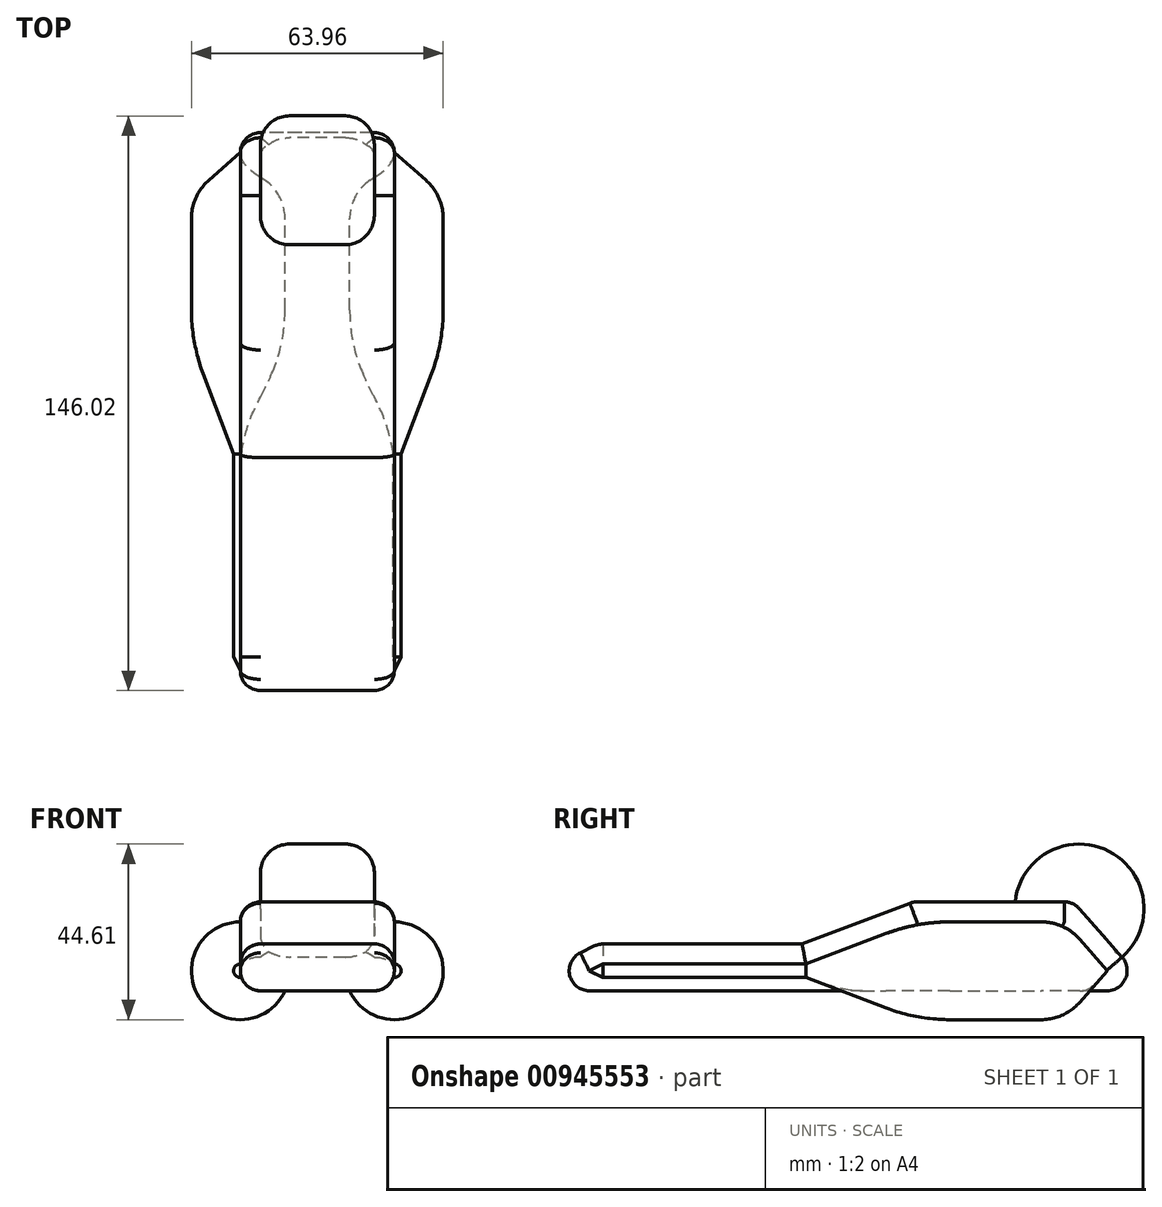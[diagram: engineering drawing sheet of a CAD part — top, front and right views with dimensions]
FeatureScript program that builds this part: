
annotation { "Feature Type Name" : "Feature", "Feature Type Description" : "" }
export const myFeature = defineFeature(function(context is Context, id is Id, definition is map)
    precondition{}
    {
        {
            var Q0;
            Q0=qCreatedBy(makeId("Right.planeOp"),FACE);
            var sketch = newSketch(context, id + "F0", { "sketchPlane" : qUnion([Q0])});
            skLineSegment(sketch, "E0", {"start": v(-69.01, 0) * mm, "end": v(-59.28, 4.77) * mm});
            skLineSegment(sketch, "E1", {"start": v(-59.28, 4.77) * mm, "end": v(-7.5, 4.77) * mm});
            skLineSegment(sketch, "E2", {"start": v(-7.5, 4.77) * mm, "end": v(20.73, 15.48) * mm});
            skLineSegment(sketch, "E3", {"start": v(20.73, 15.48) * mm, "end": v(61.42, 15.48) * mm});
            skLineSegment(sketch, "E4", {"start": v(61.42, 15.48) * mm, "end": v(75.05, 0) * mm});
            skLineSegment(sketch, "E5", {"start": v(75.05, 0) * mm, "end": v(75.05, -7.1) * mm});
            skLineSegment(sketch, "E6", {"start": v(75.05, -7.1) * mm, "end": v(-74.66, -7.1) * mm});
            skLineSegment(sketch, "E7", {"start": v(-74.66, -7.1) * mm, "end": v(-69.01, 0) * mm});
            skSolve(sketch);
        }
        {
            var Q0;
            Q0=makeQuery(id+"F0.imprint","IMPRINT",FACE,{"disambiguationData":[TD([[makeQuery(id+"F0.imprint","IMPRINT",EDGE,{"derivedFrom":sQuery(id+"F0.wireOp",EDGE,"E0")}),-1.0]])]});
            extrude(context, id + "F1", {"entities" : qUnion([Q0]), "depth" : 39.12 * mm, "offsetDistance" : 25.4 * mm});
        }
        {
            var Q0;
            Q0=makeQuery(id+"F1.opExtrude","CAP_EDGE",EDGE,{"disambiguationData":[OSD([sQuery(id+"F0.wireOp",EDGE,"E2")])],"isStart":false});
            fillet(context, id + "F2", {"entities" : qUnion([Q0]), "radius" : 5.08 * mm, "tangentPropagation" : true, "allowEdgeOverflow" : false});
        }
        {
            var Q0;
            Q0=makeQuery(id+"F1.opExtrude","CAP_EDGE",EDGE,{"disambiguationData":[OSD([sQuery(id+"F0.wireOp",EDGE,"E2")])],"isStart":true});
            fillet(context, id + "F3", {"entities" : qUnion([Q0]), "radius" : 5.08 * mm, "tangentPropagation" : true, "allowEdgeOverflow" : false});
        }
        {
            var Q0;
            Q0=makeQuery(id+"F1.opExtrude","SWEPT_EDGE",EDGE,{"disambiguationData":[OSD([sQuery(id+"F0.wireOp",EDGE,"E2"),sQuery(id+"F0.wireOp",EDGE,"E3")])]});
            fillet(context, id + "F4", {"entities" : qUnion([Q0]), "radius" : 5.08 * mm, "tangentPropagation" : true, "allowEdgeOverflow" : false});
        }
        {
            var Q0;
            Q0=makeQuery(id+"F1.opExtrude","CAP_EDGE",EDGE,{"disambiguationData":[OSD([sQuery(id+"F0.wireOp",EDGE,"E1")])],"isStart":true});
            fillet(context, id + "F5", {"entities" : qUnion([Q0]), "radius" : 5.08 * mm, "tangentPropagation" : true, "allowEdgeOverflow" : false});
        }
        {
            var Q0;
            Q0=makeQuery(id+"F5.opFillet","BLEND_EDGE",EDGE,{"blendedFrom":[makeQuery(id+"F1.opExtrude","CAP_EDGE",EDGE,{"disambiguationData":[OSD([sQuery(id+"F0.wireOp",EDGE,"E1")])],"isStart":true}),makeQuery(id+"F1.opExtrude","SWEPT_FACE",FACE,{"disambiguationData":[OSD([sQuery(id+"F0.wireOp",EDGE,"E0")])]})],"blendedInto":[makeQuery(id+"F1.opExtrude","SWEPT_FACE",FACE,{"disambiguationData":[OSD([sQuery(id+"F0.wireOp",EDGE,"E0")])]})]});
            fillet(context, id + "F6", {"entities" : qUnion([Q0]), "radius" : 5.08 * mm, "tangentPropagation" : true, "allowEdgeOverflow" : false});
        }
        {
            var Q0;
            Q0=makeQuery(id+"F6.opFillet","BLEND_EDGE",EDGE,{"blendedFrom":[makeQuery(id+"F5.opFillet","BLEND_EDGE",EDGE,{"blendedFrom":[makeQuery(id+"F1.opExtrude","CAP_EDGE",EDGE,{"disambiguationData":[OSD([sQuery(id+"F0.wireOp",EDGE,"E1")])],"isStart":true}),makeQuery(id+"F1.opExtrude","SWEPT_FACE",FACE,{"disambiguationData":[OSD([sQuery(id+"F0.wireOp",EDGE,"E0")])]})],"blendedInto":[makeQuery(id+"F1.opExtrude","SWEPT_FACE",FACE,{"disambiguationData":[OSD([sQuery(id+"F0.wireOp",EDGE,"E0")])]})]}),makeQuery(id+"F1.opExtrude","SWEPT_FACE",FACE,{"disambiguationData":[OSD([sQuery(id+"F0.wireOp",EDGE,"E7")])]})],"blendedInto":[makeQuery(id+"F1.opExtrude","SWEPT_FACE",FACE,{"disambiguationData":[OSD([sQuery(id+"F0.wireOp",EDGE,"E7")])]})]});
            fillet(context, id + "F7", {"entities" : qUnion([Q0]), "radius" : 5.08 * mm, "tangentPropagation" : true, "allowEdgeOverflow" : false});
        }
        {
            var Q0;
            Q0=makeQuery(id+"F1.opExtrude","CAP_EDGE",EDGE,{"disambiguationData":[OSD([sQuery(id+"F0.wireOp",EDGE,"E1")])],"isStart":false});
            fillet(context, id + "F8", {"entities" : qUnion([Q0]), "radius" : 5.08 * mm, "tangentPropagation" : true, "allowEdgeOverflow" : false});
        }
        {
            var Q0;
            Q0=makeQuery(id+"F1.opExtrude","SWEPT_EDGE",EDGE,{"disambiguationData":[OSD([sQuery(id+"F0.wireOp",EDGE,"E3"),sQuery(id+"F0.wireOp",EDGE,"E4")])]});
            fillet(context, id + "F9", {"entities" : qUnion([Q0]), "radius" : 5.08 * mm, "tangentPropagation" : true, "allowEdgeOverflow" : false});
        }
        {
            var Q0;
            Q0=makeQuery(id+"F1.opExtrude","SWEPT_EDGE",EDGE,{"disambiguationData":[OSD([sQuery(id+"F0.wireOp",EDGE,"E5"),sQuery(id+"F0.wireOp",EDGE,"E6")])]});
            fillet(context, id + "F10", {"entities" : qUnion([Q0]), "radius" : 5.08 * mm, "tangentPropagation" : true, "allowEdgeOverflow" : false});
        }
        {
            var Q0;
            Q0=makeQuery(id+"F1.opExtrude","CAP_EDGE",EDGE,{"disambiguationData":[OSD([sQuery(id+"F0.wireOp",EDGE,"E6")])],"isStart":false});
            fillet(context, id + "F11", {"entities" : qUnion([Q0]), "radius" : 5.08 * mm, "tangentPropagation" : true, "allowEdgeOverflow" : false});
        }
        {
            var Q0;
            Q0=makeQuery(id+"F1.opExtrude","CAP_FACE",FACE,{"disambiguationData":[OSD([sQuery(id+"F0.wireOp",EDGE,"E0"),sQuery(id+"F0.wireOp",EDGE,"E1"),sQuery(id+"F0.wireOp",EDGE,"E2"),sQuery(id+"F0.wireOp",EDGE,"E3"),sQuery(id+"F0.wireOp",EDGE,"E4"),sQuery(id+"F0.wireOp",EDGE,"E5"),sQuery(id+"F0.wireOp",EDGE,"E6"),sQuery(id+"F0.wireOp",EDGE,"E7")])],"isStart":true});
            var Q1;
            {var subQ0=sQuery(id+"F0.wireOp",EDGE,"E6");Q1=makeQuery(id+"F11.opFillet","BLEND_EDGE",EDGE,{"blendedFrom":[makeQuery(id+"F1.opExtrude","CAP_EDGE",EDGE,{"disambiguationData":[OSD([subQ0])],"isStart":true}),makeQuery(id+"F1.opExtrude","CAP_FACE",FACE,{"disambiguationData":[OSD([sQuery(id+"F0.wireOp",EDGE,"E0"),sQuery(id+"F0.wireOp",EDGE,"E1"),sQuery(id+"F0.wireOp",EDGE,"E2"),sQuery(id+"F0.wireOp",EDGE,"E3"),sQuery(id+"F0.wireOp",EDGE,"E4"),sQuery(id+"F0.wireOp",EDGE,"E5"),subQ0,sQuery(id+"F0.wireOp",EDGE,"E7")])],"isStart":true})],"blendedInto":[makeQuery(id+"F1.opExtrude","CAP_FACE",FACE,{"disambiguationData":[OSD([sQuery(id+"F0.wireOp",EDGE,"E0"),sQuery(id+"F0.wireOp",EDGE,"E1"),sQuery(id+"F0.wireOp",EDGE,"E2"),sQuery(id+"F0.wireOp",EDGE,"E3"),sQuery(id+"F0.wireOp",EDGE,"E4"),sQuery(id+"F0.wireOp",EDGE,"E5"),subQ0,sQuery(id+"F0.wireOp",EDGE,"E7")])],"isStart":true})]});}
            revolve(context, id + "F12", {"operationType" : NewBodyOperationType.ADD, "surfaceOperationType" : NewSurfaceOperationType.NEW, "entities" : qUnion([Q0]), "axis" : qUnion([Q1]), "revolveType" : RevolveType.FULL});
        }
        {
            var Q0;
            Q0=makeQuery(id+"F1.opExtrude","CAP_FACE",FACE,{"disambiguationData":[OSD([sQuery(id+"F0.wireOp",EDGE,"E0"),sQuery(id+"F0.wireOp",EDGE,"E1"),sQuery(id+"F0.wireOp",EDGE,"E2"),sQuery(id+"F0.wireOp",EDGE,"E3"),sQuery(id+"F0.wireOp",EDGE,"E4"),sQuery(id+"F0.wireOp",EDGE,"E5"),sQuery(id+"F0.wireOp",EDGE,"E6"),sQuery(id+"F0.wireOp",EDGE,"E7")])],"isStart":false});
            var Q1;
            {var subQ0=sQuery(id+"F0.wireOp",EDGE,"E6");Q1=makeQuery(id+"F11.opFillet","BLEND_EDGE",EDGE,{"blendedFrom":[makeQuery(id+"F1.opExtrude","CAP_EDGE",EDGE,{"disambiguationData":[OSD([subQ0])],"isStart":false}),makeQuery(id+"F1.opExtrude","CAP_FACE",FACE,{"disambiguationData":[OSD([sQuery(id+"F0.wireOp",EDGE,"E0"),sQuery(id+"F0.wireOp",EDGE,"E1"),sQuery(id+"F0.wireOp",EDGE,"E2"),sQuery(id+"F0.wireOp",EDGE,"E3"),sQuery(id+"F0.wireOp",EDGE,"E4"),sQuery(id+"F0.wireOp",EDGE,"E5"),subQ0,sQuery(id+"F0.wireOp",EDGE,"E7")])],"isStart":false})],"blendedInto":[makeQuery(id+"F1.opExtrude","CAP_FACE",FACE,{"disambiguationData":[OSD([sQuery(id+"F0.wireOp",EDGE,"E0"),sQuery(id+"F0.wireOp",EDGE,"E1"),sQuery(id+"F0.wireOp",EDGE,"E2"),sQuery(id+"F0.wireOp",EDGE,"E3"),sQuery(id+"F0.wireOp",EDGE,"E4"),sQuery(id+"F0.wireOp",EDGE,"E5"),subQ0,sQuery(id+"F0.wireOp",EDGE,"E7")])],"isStart":false})]});}
            revolve(context, id + "F13", {"operationType" : NewBodyOperationType.ADD, "surfaceOperationType" : NewSurfaceOperationType.NEW, "entities" : qUnion([Q0]), "axis" : qUnion([Q1]), "revolveType" : RevolveType.FULL});
        }
        {
            var Q0;
            {var subQ0=sQuery(id+"F0.wireOp",EDGE,"E7");var subQ1=sQuery(id+"F0.wireOp",EDGE,"E6");var subQ2=sQuery(id+"F0.wireOp",EDGE,"E5");var subQ3=sQuery(id+"F0.wireOp",EDGE,"E4");var subQ4=sQuery(id+"F0.wireOp",EDGE,"E3");var subQ5=sQuery(id+"F0.wireOp",EDGE,"E2");var subQ6=sQuery(id+"F0.wireOp",EDGE,"E1");var subQ7=sQuery(id+"F0.wireOp",EDGE,"E0");Q0=makeQuery(id+"F12.opRevolve","SWEPT_EDGE",EDGE,{"disambiguationData":[OSD([subQ7,subQ6,subQ5,subQ4,subQ3,subQ2,subQ1,subQ0]),TDD([makeQuery(id+"F4.opFillet","BLEND_VERTEX",VERTEX,{"blendedFrom":[makeQuery(id+"F3.opFillet","BLEND_EDGE",EDGE,{"blendedFrom":[makeQuery(id+"F1.opExtrude","CAP_EDGE",EDGE,{"disambiguationData":[OSD([subQ5])],"isStart":true}),makeQuery(id+"F1.opExtrude","SWEPT_FACE",FACE,{"disambiguationData":[OSD([subQ4])]})],"blendedInto":[makeQuery(id+"F1.opExtrude","SWEPT_FACE",FACE,{"disambiguationData":[OSD([subQ4])]})]}),makeQuery(id+"F1.opExtrude","CAP_EDGE",EDGE,{"disambiguationData":[OSD([subQ4])],"isStart":true}),makeQuery(id+"F3.opFillet","BLEND_FACE",FACE,{"disambiguationData":[OSD([subQ5])]}),makeQuery(id+"F1.opExtrude","CAP_FACE",FACE,{"disambiguationData":[OSD([subQ7,subQ6,subQ5,subQ4,subQ3,subQ2,subQ1,subQ0])],"isStart":true})],"blendedInto":[makeQuery(id+"F3.opFillet","BLEND_FACE",FACE,{"disambiguationData":[OSD([subQ5])]}),makeQuery(id+"F1.opExtrude","CAP_FACE",FACE,{"disambiguationData":[OSD([subQ7,subQ6,subQ5,subQ4,subQ3,subQ2,subQ1,subQ0])],"isStart":true})]})])]});}
            fillet(context, id + "F14", {"entities" : qUnion([Q0]), "radius" : 45.74 * mm, "tangentPropagation" : true, "allowEdgeOverflow" : false});
        }
        {
            var Q0;
            {var subQ0=sQuery(id+"F0.wireOp",EDGE,"E7");var subQ1=sQuery(id+"F0.wireOp",EDGE,"E6");var subQ2=sQuery(id+"F0.wireOp",EDGE,"E5");var subQ3=sQuery(id+"F0.wireOp",EDGE,"E4");var subQ4=sQuery(id+"F0.wireOp",EDGE,"E3");var subQ5=sQuery(id+"F0.wireOp",EDGE,"E2");var subQ6=sQuery(id+"F0.wireOp",EDGE,"E1");var subQ7=sQuery(id+"F0.wireOp",EDGE,"E0");var subQ8=makeQuery(id+"F1.opExtrude","CAP_EDGE",EDGE,{"disambiguationData":[OSD([subQ4])],"isStart":true});Q0=makeQuery(id+"F12.opRevolve","SWEPT_EDGE",EDGE,{"disambiguationData":[OSD([subQ7,subQ6,subQ5,subQ4,subQ3,subQ2,subQ1,subQ0]),TDD([makeQuery(id+"F9.opFillet","BLEND_VERTEX",VERTEX,{"blendedFrom":[makeQuery(id+"F1.opExtrude","CAP_EDGE",EDGE,{"disambiguationData":[OSD([subQ3])],"isStart":true}),makeQuery(id+"F4.opFillet","BLEND_EDGE",EDGE,{"blendedFrom":[subQ8,makeQuery(id+"F1.opExtrude","SWEPT_FACE",FACE,{"disambiguationData":[OSD([subQ3])]})],"blendedInto":[makeQuery(id+"F1.opExtrude","SWEPT_FACE",FACE,{"disambiguationData":[OSD([subQ3])]})]}),makeQuery(id+"F4.opFillet","BLEND_FACE",FACE,{"disambiguationData":[OSD([subQ4]),TDD([subQ8])]}),makeQuery(id+"F1.opExtrude","CAP_FACE",FACE,{"disambiguationData":[OSD([subQ7,subQ6,subQ5,subQ4,subQ3,subQ2,subQ1,subQ0])],"isStart":true})],"blendedInto":[makeQuery(id+"F4.opFillet","BLEND_FACE",FACE,{"disambiguationData":[OSD([subQ4]),TDD([subQ8])]}),makeQuery(id+"F1.opExtrude","CAP_FACE",FACE,{"disambiguationData":[OSD([subQ7,subQ6,subQ5,subQ4,subQ3,subQ2,subQ1,subQ0])],"isStart":true})]})])]});}
            fillet(context, id + "F15", {"entities" : qUnion([Q0]), "radius" : 13.04 * mm, "tangentPropagation" : true, "allowEdgeOverflow" : false});
        }
        {
            var Q0;
            {var subQ0=sQuery(id+"F0.wireOp",EDGE,"E7");var subQ1=sQuery(id+"F0.wireOp",EDGE,"E6");var subQ2=sQuery(id+"F0.wireOp",EDGE,"E5");var subQ3=sQuery(id+"F0.wireOp",EDGE,"E4");var subQ4=sQuery(id+"F0.wireOp",EDGE,"E3");var subQ5=sQuery(id+"F0.wireOp",EDGE,"E2");var subQ6=sQuery(id+"F0.wireOp",EDGE,"E1");var subQ7=sQuery(id+"F0.wireOp",EDGE,"E0");Q0=makeQuery(id+"F12.opRevolve","SWEPT_EDGE",EDGE,{"disambiguationData":[OSD([subQ7,subQ6,subQ5,subQ4,subQ3,subQ2,subQ1,subQ0]),TDD([makeQuery(id+"F6.opFillet","BLEND_VERTEX",VERTEX,{"blendedFrom":[makeQuery(id+"F5.opFillet","BLEND_EDGE",EDGE,{"blendedFrom":[makeQuery(id+"F1.opExtrude","CAP_EDGE",EDGE,{"disambiguationData":[OSD([subQ6])],"isStart":true}),makeQuery(id+"F1.opExtrude","SWEPT_FACE",FACE,{"disambiguationData":[OSD([subQ7])]})],"blendedInto":[makeQuery(id+"F1.opExtrude","SWEPT_FACE",FACE,{"disambiguationData":[OSD([subQ7])]})]}),makeQuery(id+"F5.opFillet","BLEND_FACE",FACE,{"disambiguationData":[OSD([subQ6])]}),makeQuery(id+"F1.opExtrude","CAP_FACE",FACE,{"disambiguationData":[OSD([subQ7,subQ6,subQ5,subQ4,subQ3,subQ2,subQ1,subQ0])],"isStart":true})],"blendedInto":[makeQuery(id+"F5.opFillet","BLEND_FACE",FACE,{"disambiguationData":[OSD([subQ6])]}),makeQuery(id+"F1.opExtrude","CAP_FACE",FACE,{"disambiguationData":[OSD([subQ7,subQ6,subQ5,subQ4,subQ3,subQ2,subQ1,subQ0])],"isStart":true})]})])]});}
            fillet(context, id + "F16", {"entities" : qUnion([Q0]), "radius" : 0.38 * mm, "tangentPropagation" : true, "allowEdgeOverflow" : false});
        }
        {
            var Q0;
            {var subQ0=sQuery(id+"F0.wireOp",EDGE,"E7");var subQ1=sQuery(id+"F0.wireOp",EDGE,"E6");var subQ2=sQuery(id+"F0.wireOp",EDGE,"E5");var subQ3=sQuery(id+"F0.wireOp",EDGE,"E4");var subQ4=sQuery(id+"F0.wireOp",EDGE,"E3");var subQ5=sQuery(id+"F0.wireOp",EDGE,"E2");var subQ6=sQuery(id+"F0.wireOp",EDGE,"E1");var subQ7=sQuery(id+"F0.wireOp",EDGE,"E0");Q0=makeQuery(id+"F13.opRevolve","SWEPT_EDGE",EDGE,{"disambiguationData":[OSD([subQ7,subQ6,subQ5,subQ4,subQ3,subQ2,subQ1,subQ0]),TDD([makeQuery(id+"F4.opFillet","BLEND_VERTEX",VERTEX,{"blendedFrom":[makeQuery(id+"F2.opFillet","BLEND_EDGE",EDGE,{"blendedFrom":[makeQuery(id+"F1.opExtrude","CAP_EDGE",EDGE,{"disambiguationData":[OSD([subQ5])],"isStart":false}),makeQuery(id+"F1.opExtrude","SWEPT_FACE",FACE,{"disambiguationData":[OSD([subQ4])]})],"blendedInto":[makeQuery(id+"F1.opExtrude","SWEPT_FACE",FACE,{"disambiguationData":[OSD([subQ4])]})]}),makeQuery(id+"F1.opExtrude","CAP_EDGE",EDGE,{"disambiguationData":[OSD([subQ4])],"isStart":false}),makeQuery(id+"F2.opFillet","BLEND_FACE",FACE,{"disambiguationData":[OSD([subQ5])]}),makeQuery(id+"F1.opExtrude","CAP_FACE",FACE,{"disambiguationData":[OSD([subQ7,subQ6,subQ5,subQ4,subQ3,subQ2,subQ1,subQ0])],"isStart":false})],"blendedInto":[makeQuery(id+"F2.opFillet","BLEND_FACE",FACE,{"disambiguationData":[OSD([subQ5])]}),makeQuery(id+"F1.opExtrude","CAP_FACE",FACE,{"disambiguationData":[OSD([subQ7,subQ6,subQ5,subQ4,subQ3,subQ2,subQ1,subQ0])],"isStart":false})]})])]});}
            fillet(context, id + "F17", {"entities" : qUnion([Q0]), "radius" : 45.74 * mm, "tangentPropagation" : true, "allowEdgeOverflow" : false});
        }
        {
            var Q0;
            {var subQ0=sQuery(id+"F0.wireOp",EDGE,"E7");var subQ1=sQuery(id+"F0.wireOp",EDGE,"E6");var subQ2=sQuery(id+"F0.wireOp",EDGE,"E5");var subQ3=sQuery(id+"F0.wireOp",EDGE,"E4");var subQ4=sQuery(id+"F0.wireOp",EDGE,"E3");var subQ5=sQuery(id+"F0.wireOp",EDGE,"E2");var subQ6=sQuery(id+"F0.wireOp",EDGE,"E1");var subQ7=sQuery(id+"F0.wireOp",EDGE,"E0");var subQ8=makeQuery(id+"F1.opExtrude","CAP_EDGE",EDGE,{"disambiguationData":[OSD([subQ4])],"isStart":false});Q0=makeQuery(id+"F13.opRevolve","SWEPT_EDGE",EDGE,{"disambiguationData":[OSD([subQ7,subQ6,subQ5,subQ4,subQ3,subQ2,subQ1,subQ0]),TDD([makeQuery(id+"F9.opFillet","BLEND_VERTEX",VERTEX,{"blendedFrom":[makeQuery(id+"F1.opExtrude","CAP_EDGE",EDGE,{"disambiguationData":[OSD([subQ3])],"isStart":false}),makeQuery(id+"F4.opFillet","BLEND_EDGE",EDGE,{"blendedFrom":[subQ8,makeQuery(id+"F1.opExtrude","SWEPT_FACE",FACE,{"disambiguationData":[OSD([subQ3])]})],"blendedInto":[makeQuery(id+"F1.opExtrude","SWEPT_FACE",FACE,{"disambiguationData":[OSD([subQ3])]})]}),makeQuery(id+"F4.opFillet","BLEND_FACE",FACE,{"disambiguationData":[OSD([subQ4]),TDD([subQ8])]}),makeQuery(id+"F1.opExtrude","CAP_FACE",FACE,{"disambiguationData":[OSD([subQ7,subQ6,subQ5,subQ4,subQ3,subQ2,subQ1,subQ0])],"isStart":false})],"blendedInto":[makeQuery(id+"F4.opFillet","BLEND_FACE",FACE,{"disambiguationData":[OSD([subQ4]),TDD([subQ8])]}),makeQuery(id+"F1.opExtrude","CAP_FACE",FACE,{"disambiguationData":[OSD([subQ7,subQ6,subQ5,subQ4,subQ3,subQ2,subQ1,subQ0])],"isStart":false})]})])]});}
            fillet(context, id + "F18", {"entities" : qUnion([Q0]), "radius" : 13.04 * mm, "tangentPropagation" : true, "allowEdgeOverflow" : false});
        }
        {
            var Q0;
            Q0=makeQuery(id+"F1.opExtrude","SWEPT_FACE",FACE,{"disambiguationData":[OSD([sQuery(id+"F0.wireOp",EDGE,"E4")])]});
            var Q1;
            {var subQ0=sQuery(id+"F0.wireOp",EDGE,"E4");Q1=makeQuery(id+"F9.opFillet","BLEND_EDGE",EDGE,{"blendedFrom":[makeQuery(id+"F1.opExtrude","SWEPT_EDGE",EDGE,{"disambiguationData":[OSD([sQuery(id+"F0.wireOp",EDGE,"E3"),subQ0])]}),makeQuery(id+"F1.opExtrude","SWEPT_FACE",FACE,{"disambiguationData":[OSD([subQ0])]})],"blendedInto":[makeQuery(id+"F1.opExtrude","SWEPT_FACE",FACE,{"disambiguationData":[OSD([subQ0])]})]});}
            revolve(context, id + "F19", {"operationType" : NewBodyOperationType.ADD, "surfaceOperationType" : NewSurfaceOperationType.NEW, "entities" : qUnion([Q0]), "axis" : qUnion([Q1]), "revolveType" : RevolveType.FULL});
        }
        {
            var Q0;
            {var subQ0=sQuery(id+"F0.wireOp",EDGE,"E4");var subQ1=makeQuery(id+"F1.opExtrude","CAP_EDGE",EDGE,{"disambiguationData":[OSD([subQ0])],"isStart":false});var subQ2=sQuery(id+"F0.wireOp",EDGE,"E5");Q0=makeQuery(id+"F19.opRevolve","SWEPT_EDGE",EDGE,{"disambiguationData":[OSD([subQ0,subQ2]),TDD([makeQuery(id+"F11.opFillet","BLEND_VERTEX",VERTEX,{"blendedFrom":[makeQuery(id+"F1.opExtrude","SWEPT_EDGE",EDGE,{"disambiguationData":[OSD([subQ0,subQ2])]}),makeQuery(id+"F9.opFillet","BLEND_EDGE",EDGE,{"blendedFrom":[subQ1,makeQuery(id+"F1.opExtrude","SWEPT_FACE",FACE,{"disambiguationData":[OSD([subQ2])]})],"blendedInto":[makeQuery(id+"F1.opExtrude","SWEPT_FACE",FACE,{"disambiguationData":[OSD([subQ2])]})]}),makeQuery(id+"F1.opExtrude","SWEPT_FACE",FACE,{"disambiguationData":[OSD([subQ0])]}),makeQuery(id+"F9.opFillet","BLEND_FACE",FACE,{"disambiguationData":[OSD([subQ0]),TDD([subQ1])]})],"blendedInto":[makeQuery(id+"F1.opExtrude","SWEPT_FACE",FACE,{"disambiguationData":[OSD([subQ0])]}),makeQuery(id+"F9.opFillet","BLEND_FACE",FACE,{"disambiguationData":[OSD([subQ0]),TDD([subQ1])]})]})])]});}
            fillet(context, id + "F20", {"entities" : qUnion([Q0]), "radius" : 7.36 * mm, "tangentPropagation" : true, "allowEdgeOverflow" : false});
        }
        {
            var Q0;
            {var subQ0=sQuery(id+"F0.wireOp",EDGE,"E4");var subQ1=makeQuery(id+"F1.opExtrude","CAP_EDGE",EDGE,{"disambiguationData":[OSD([subQ0])],"isStart":true});var subQ2=sQuery(id+"F0.wireOp",EDGE,"E5");Q0=makeQuery(id+"F19.opRevolve","SWEPT_EDGE",EDGE,{"disambiguationData":[OSD([subQ0,subQ2]),TDD([makeQuery(id+"F11.opFillet","BLEND_VERTEX",VERTEX,{"blendedFrom":[makeQuery(id+"F1.opExtrude","SWEPT_EDGE",EDGE,{"disambiguationData":[OSD([subQ0,subQ2])]}),makeQuery(id+"F9.opFillet","BLEND_EDGE",EDGE,{"blendedFrom":[subQ1,makeQuery(id+"F1.opExtrude","SWEPT_FACE",FACE,{"disambiguationData":[OSD([subQ2])]})],"blendedInto":[makeQuery(id+"F1.opExtrude","SWEPT_FACE",FACE,{"disambiguationData":[OSD([subQ2])]})]}),makeQuery(id+"F1.opExtrude","SWEPT_FACE",FACE,{"disambiguationData":[OSD([subQ0])]}),makeQuery(id+"F9.opFillet","BLEND_FACE",FACE,{"disambiguationData":[OSD([subQ0]),TDD([subQ1])]})],"blendedInto":[makeQuery(id+"F1.opExtrude","SWEPT_FACE",FACE,{"disambiguationData":[OSD([subQ0])]}),makeQuery(id+"F9.opFillet","BLEND_FACE",FACE,{"disambiguationData":[OSD([subQ0]),TDD([subQ1])]})]})])]});}
            fillet(context, id + "F21", {"entities" : qUnion([Q0]), "radius" : 7.36 * mm, "tangentPropagation" : true, "allowEdgeOverflow" : false});
        }
    });
